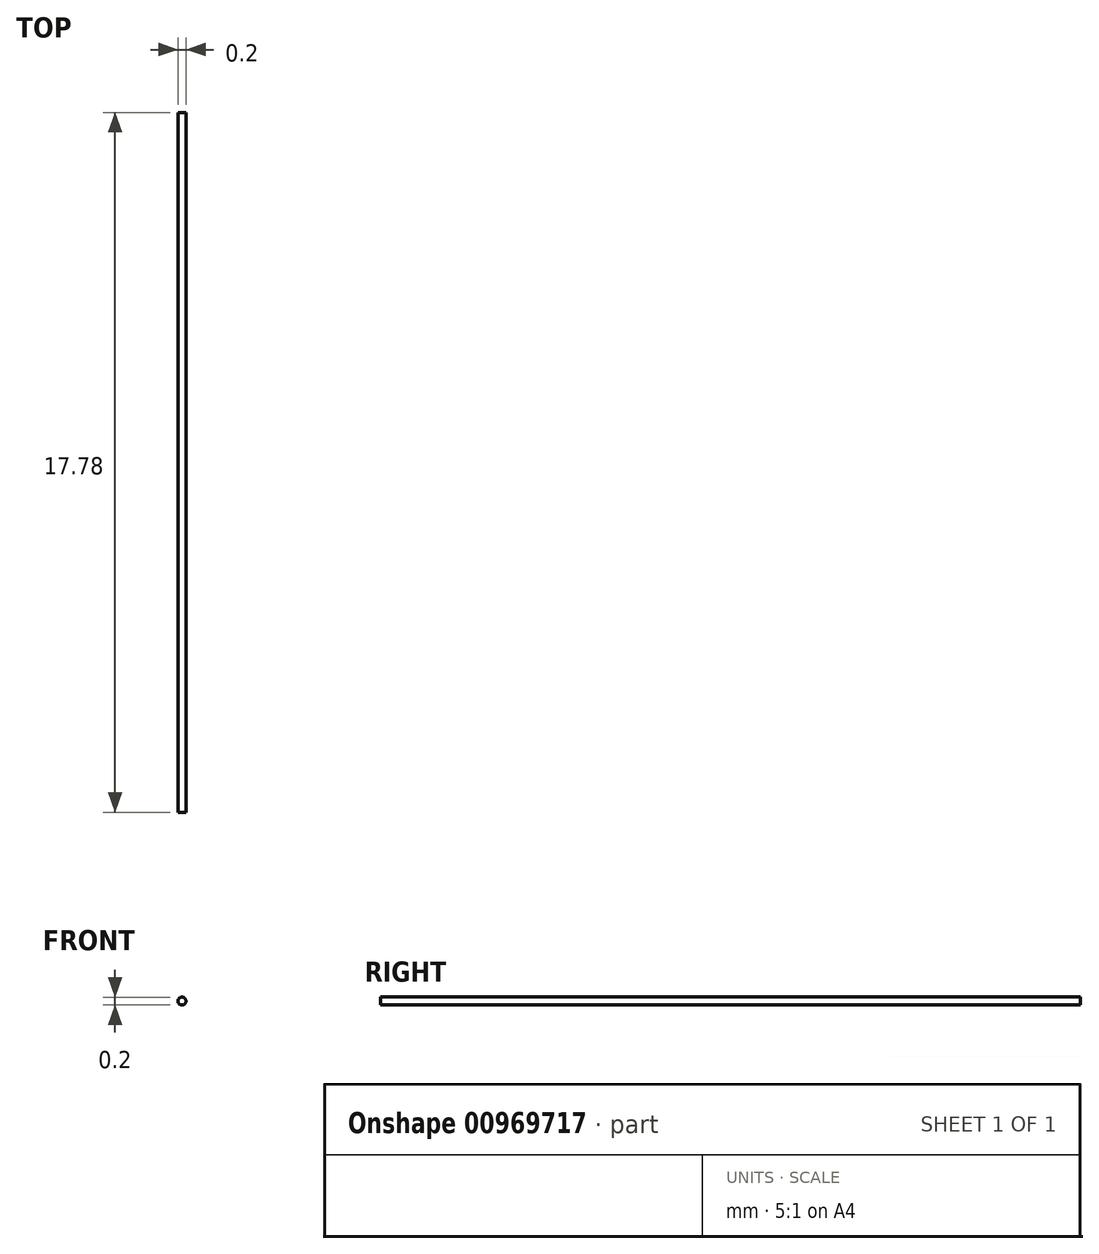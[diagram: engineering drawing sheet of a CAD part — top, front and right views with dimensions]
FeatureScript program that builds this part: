
annotation { "Feature Type Name" : "Feature", "Feature Type Description" : "" }
export const myFeature = defineFeature(function(context is Context, id is Id, definition is map)
    precondition{}
    {
        {
            var Q0;
            Q0=qCreatedBy(makeId("Front.planeOp"),FACE);
            var sketch = newSketch(context, id + "F0", { "sketchPlane" : qUnion([Q0])});
            skCircle(sketch, "E0", {"center": v(0, 0) * mm, "radius": 0.1 * mm});
            skSolve(sketch);
        }
        {
            var Q0;
            Q0=makeQuery(id+"F0.imprint","IMPRINT",FACE,{"disambiguationData":[TD([[makeQuery(id+"F0.imprint","IMPRINT",EDGE,{"derivedFrom":sQuery(id+"F0.wireOp",EDGE,"E0")}),1.0]])]});
            extrude(context, id + "F1", {"entities" : qUnion([Q0]), "depth" : 17.78 * mm, "offsetDistance" : 25.4 * mm});
        }
    });
